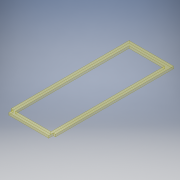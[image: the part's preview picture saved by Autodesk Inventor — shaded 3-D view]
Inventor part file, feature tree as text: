
AUTODESK INVENTOR PART (.ipt)
format: ipt  version: 2018.1 (Build 221171000, 171)  size: 135,680 bytes
history: native  units: mm
features: other x1, plane x1, extrude x1, sketch x1
ambient origin geometry x8: Origin, YZ Plane, XZ Plane, XY Plane, X Axis, Y Axis, Z Axis, Center Point
bodies: Solid1 (feature_tree)
feature tree (4):
  parser-record x1  (decoder bookkeeping rows leaked as tree rows — omitted from the tree; the rows remain in map.json)
  plane  "Work Plane1"
  extrude  "Extrusion2"  Depth=273.0mm
  sketch  "Sketch2"  dims[d4=99.0mm d5=273.0mm d6=5.5mm d7=5.5mm d8=5.0mm d9=79.0mm d10=253.0mm d11=10.0mm d12=10.0mm d13=5.0mm d14=10.0mm d15=5.0mm d16=10.0mm d17=5.0mm d18=0.0mm]
note: 1 file-system path scrubbed to <path> (originals preserved in map.json)
